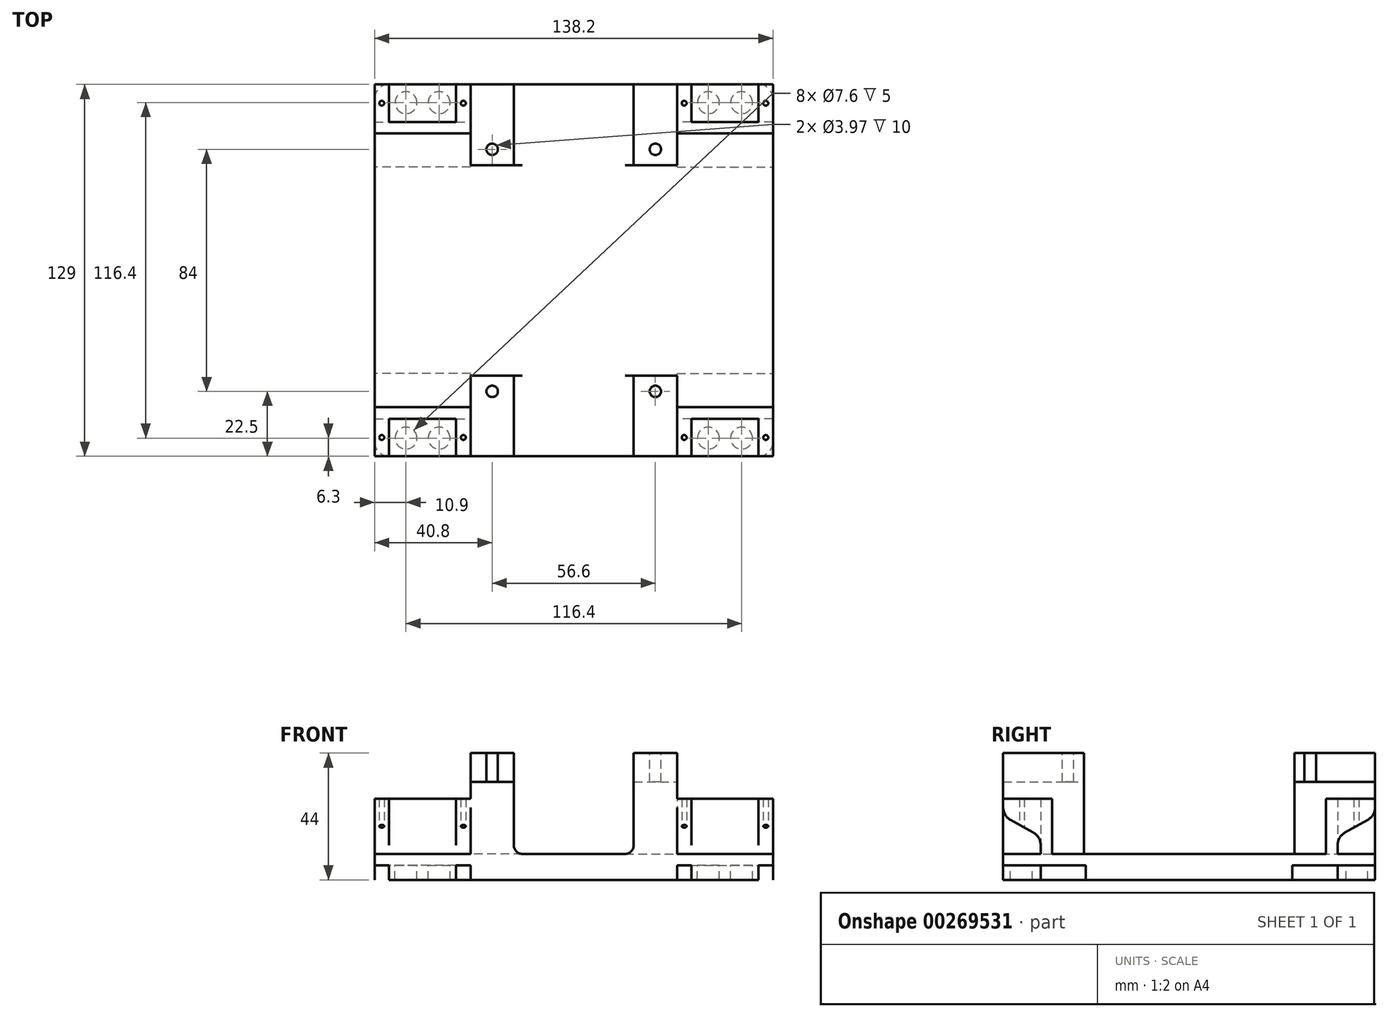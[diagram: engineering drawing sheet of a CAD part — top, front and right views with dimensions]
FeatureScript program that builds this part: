
annotation { "Feature Type Name" : "Feature", "Feature Type Description" : "" }
export const myFeature = defineFeature(function(context is Context, id is Id, definition is map)
    precondition{}
    {
        {
            var Q0;
            Q0=qCreatedBy(makeId("Top.planeOp"),FACE);
            var sketch = newSketch(context, id + "F0", { "sketchPlane" : qUnion([Q0])});
            skLineSegment(sketch, "E0.bottom", {"start": v(16.65, 8.5) * mm, "end": v(-16.65, 8.5) * mm});
            skLineSegment(sketch, "E0.top", {"start": v(16.65, -8.5) * mm, "end": v(-16.65, -8.5) * mm});
            skLineSegment(sketch, "E0.left", {"start": v(16.65, 8.5) * mm, "end": v(16.65, -8.5) * mm});
            skLineSegment(sketch, "E0.right", {"start": v(-16.65, 8.5) * mm, "end": v(-16.65, -8.5) * mm});
            skPoint(sketch, "E0.middle", {"position": v(0, 0) * mm});
            skLineSegment(sketch, "E1", {"start": v(11.65, -8.5) * mm, "end": v(11.65, 8.5) * mm});
            skLineSegment(sketch, "E2", {"start": v(-11.65, -8.5) * mm, "end": v(-11.65, 8.5) * mm});
            skLineSegment(sketch, "E3", {"start": v(-11.65, 4.5) * mm, "end": v(11.65, 4.5) * mm});
            skCircle(sketch, "E4", {"center": v(14.15, -2) * mm, "radius": 0.85 * mm});
            skCircle(sketch, "E5", {"center": v(-14.15, -2) * mm, "radius": 0.85 * mm});
            skCircle(sketch, "E6", {"center": v(-5.75, -2.2) * mm, "radius": 3.8 * mm});
            skCircle(sketch, "E7.MirrorC", {"center": v(5.75, -2.2) * mm, "radius": 3.8 * mm});
            skLineSegment(sketch, "E8.bottom", {"start": v(-16.65, 8.5) * mm, "end": v(-33.65, 8.5) * mm});
            skLineSegment(sketch, "E8.top", {"start": v(-16.65, -8.5) * mm, "end": v(-33.65, -8.5) * mm});
            skLineSegment(sketch, "E8.right", {"start": v(-33.65, 8.5) * mm, "end": v(-33.65, -8.5) * mm});
            skLineSegment(sketch, "E9.bottom", {"start": v(-16.65, 8.5) * mm, "end": v(16.65, 8.5) * mm});
            skLineSegment(sketch, "E9.top", {"start": v(-16.65, 25.5) * mm, "end": v(16.65, 25.5) * mm});
            skLineSegment(sketch, "E9.left", {"start": v(-16.65, 8.5) * mm, "end": v(-16.65, 25.5) * mm});
            skLineSegment(sketch, "E9.right", {"start": v(16.65, 8.5) * mm, "end": v(16.65, 25.5) * mm});
            skCircle(sketch, "E10", {"center": v(-25.15, 0) * mm, "radius": 3 * mm});
            skPoint(sketch, "E10.centerSnap0", {"position": v(-25.15, -8.5) * mm});
            skCircle(sketch, "E11", {"center": v(-8.33, 17) * mm, "radius": 3 * mm});
            skPoint(sketch, "E11.centerSnap0", {"position": v(-16.65, 17) * mm});
            skLineSegment(sketch, "E12", {"start": v(0, 25.5) * mm, "end": v(0, 8.5) * mm});
            skCircle(sketch, "E13.MirrorC", {"center": v(8.33, 17) * mm, "radius": 3 * mm});
            skSolve(sketch);
        }
        {
            var Q0;
            Q0=qCreatedBy(makeId("Front.planeOp"),FACE);
            var sketch = newSketch(context, id + "F1", { "sketchPlane" : qUnion([Q0])});
            skLineSegment(sketch, "E14.bottom", {"start": v(-16.65, 0) * mm, "end": v(16.65, 0) * mm});
            skLineSegment(sketch, "E14.top", {"start": v(-16.65, 23.2) * mm, "end": v(16.65, 23.2) * mm});
            skLineSegment(sketch, "E14.left", {"start": v(-16.65, 0) * mm, "end": v(-16.65, 23.2) * mm});
            skLineSegment(sketch, "E14.right", {"start": v(16.65, 0) * mm, "end": v(16.65, 23.2) * mm});
            skLineSegment(sketch, "E15", {"start": v(-16.65, 4) * mm, "end": v(16.65, 4) * mm});
            skLineSegment(sketch, "E16", {"start": v(11.65, 0) * mm, "end": v(11.65, 23.2) * mm});
            skLineSegment(sketch, "E17", {"start": v(-11.65, 0) * mm, "end": v(-11.65, 23.2) * mm});
            skLineSegment(sketch, "E18", {"start": v(16.65, 10) * mm, "end": v(11.65, 10) * mm});
            skLineSegment(sketch, "E19", {"start": v(-11.65, 10) * mm, "end": v(-16.65, 10) * mm});
            skLineSegment(sketch, "E20", {"start": v(11.65, 17.2) * mm, "end": v(16.65, 17.2) * mm});
            skLineSegment(sketch, "E21", {"start": v(-11.65, 17.2) * mm, "end": v(-16.65, 17.2) * mm});
            skSolve(sketch);
        }
        {
            var Q0;
            Q0=qCreatedBy(makeId("Right.planeOp"),FACE);
            var sketch = newSketch(context, id + "F2", { "sketchPlane" : qUnion([Q0])});
            skLineSegment(sketch, "E22.bottom", {"start": v(-8.5, 0) * mm, "end": v(8.5, 0) * mm});
            skLineSegment(sketch, "E22.top", {"start": v(-8.5, 23.2) * mm, "end": v(8.5, 23.2) * mm});
            skLineSegment(sketch, "E22.left", {"start": v(-8.5, 20.15) * mm, "end": v(-8.5, 23.2) * mm});
            skLineSegment(sketch, "E22.right", {"start": v(8.5, 0) * mm, "end": v(8.5, 23.2) * mm});
            skLineSegment(sketch, "E23", {"start": v(4.5, 7.05) * mm, "end": v(4.5, 0) * mm});
            skLineSegment(sketch, "E24", {"start": v(4.5, 17.2) * mm, "end": v(-8.5, 17.2) * mm});
            skLineSegment(sketch, "E25", {"start": v(4.5, 4) * mm, "end": v(-8.5, 4) * mm});
            skLineSegment(sketch, "E26", {"start": v(-8.5, 10) * mm, "end": v(4.5, 10) * mm});
            skLineSegment(sketch, "E27", {"start": v(-5.92, 15.77) * mm, "end": v(1.92, 11.43) * mm});
            skArc(sketch, "E28.filletArc", {"start": v(-8.5, 20.15) * mm, "mid": v(-7.8, 17.6) * mm, "end": v(-5.92, 15.77) * mm});
            skArc(sketch, "E29.filletArc", {"start": v(4.5, 7.05) * mm, "mid": v(3.8, 9.6) * mm, "end": v(1.92, 11.43) * mm});
            skLineSegment(sketch, "E30", {"start": v(-8.5, 20.15) * mm, "end": v(-8.5, 0) * mm});
            skSolve(sketch);
        }
        {
            var Q0;
            {var subQ0=sQuery(id+"F1.wireOp",EDGE,"E19");Q0=makeQuery(id+"F1.imprint","IMPRINT",FACE,{"disambiguationData":[TD([[makeQuery(id+"F1.imprint","IMPRINT",EDGE,{"derivedFrom":subQ0}),-1.0]])]});}
            var Q1;
            {var subQ5=sQuery(id+"F1.wireOp",EDGE,"E21");Q1=makeQuery(id+"F1.imprint","IMPRINT",FACE,{"disambiguationData":[TD([[makeQuery(id+"F1.imprint","IMPRINT",EDGE,{"derivedFrom":subQ5}),-1.0]])]});}
            var Q2;
            {var subQ3=sQuery(id+"F1.wireOp",EDGE,"E19");Q2=makeQuery(id+"F1.imprint","IMPRINT",FACE,{"disambiguationData":[TD([[makeQuery(id+"F1.imprint","IMPRINT",EDGE,{"derivedFrom":subQ3}),1.0]])]});}
            var Q3;
            {var subQ0=sQuery(id+"F1.wireOp",EDGE,"E14.left");var subQ1=sQuery(id+"F1.wireOp",EDGE,"E14.bottom");var subQ2=makeQuery(id+"F1.imprint","INTERSECT",VERTEX,{"derivedFrom":[subQ1,subQ0]});Q3=makeQuery(id+"F1.imprint","IMPRINT",FACE,{"disambiguationData":[TD([[makeQuery(id+"F1.imprint","IMPRINT",EDGE,{"disambiguationData":[TD([[subQ2,-1.0]])],"derivedFrom":subQ1}),1.0]])]});}
            var Q4;
            {var subQ0=sQuery(id+"F1.wireOp",EDGE,"E16");var subQ1=sQuery(id+"F1.wireOp",EDGE,"E14.bottom");var subQ2=makeQuery(id+"F1.imprint","INTERSECT",VERTEX,{"derivedFrom":[subQ1,subQ0]});Q4=makeQuery(id+"F1.imprint","IMPRINT",FACE,{"disambiguationData":[TD([[makeQuery(id+"F1.imprint","IMPRINT",EDGE,{"disambiguationData":[TD([[subQ2,1.0]])],"derivedFrom":subQ1}),1.0]])]});}
            var Q5;
            {var subQ0=sQuery(id+"F1.wireOp",EDGE,"E14.right");var subQ1=sQuery(id+"F1.wireOp",EDGE,"E14.bottom");var subQ2=makeQuery(id+"F1.imprint","INTERSECT",VERTEX,{"derivedFrom":[subQ1,subQ0]});Q5=makeQuery(id+"F1.imprint","IMPRINT",FACE,{"disambiguationData":[TD([[makeQuery(id+"F1.imprint","IMPRINT",EDGE,{"disambiguationData":[TD([[subQ2,1.0]])],"derivedFrom":subQ1}),1.0]])]});}
            var Q6;
            {var subQ3=sQuery(id+"F1.wireOp",EDGE,"E18");Q6=makeQuery(id+"F1.imprint","IMPRINT",FACE,{"disambiguationData":[TD([[makeQuery(id+"F1.imprint","IMPRINT",EDGE,{"derivedFrom":subQ3}),1.0]])]});}
            var Q7;
            {var subQ0=sQuery(id+"F1.wireOp",EDGE,"E18");Q7=makeQuery(id+"F1.imprint","IMPRINT",FACE,{"disambiguationData":[TD([[makeQuery(id+"F1.imprint","IMPRINT",EDGE,{"derivedFrom":subQ0}),-1.0]])]});}
            var Q8;
            {var subQ5=sQuery(id+"F1.wireOp",EDGE,"E20");Q8=makeQuery(id+"F1.imprint","IMPRINT",FACE,{"disambiguationData":[TD([[makeQuery(id+"F1.imprint","IMPRINT",EDGE,{"derivedFrom":subQ5}),1.0]])]});}
            extrude(context, id + "F3", {"entities" : qUnion([Q0, Q1, Q2, Q3, Q4, Q5, Q6, Q7, Q8]), "endBound" : BoundingType.SYMMETRIC, "depth" : 17 * mm});
        }
        {
            var Q0;
            {var subQ5=sQuery(id+"F0.wireOp",EDGE,"E3");Q0=makeQuery(id+"F0.imprint","IMPRINT",FACE,{"disambiguationData":[TD([[makeQuery(id+"F0.imprint","IMPRINT",EDGE,{"derivedFrom":subQ5}),1.0]])]});}
            extrude(context, id + "F4", {"entities" : qUnion([Q0]), "operationType" : NewBodyOperationType.ADD, "depth" : 23.2 * mm});
        }
        {
            var Q0;
            {var subQ0=sQuery(id+"F2.wireOp",EDGE,"E27");Q0=makeQuery(id+"F2.imprint","IMPRINT",FACE,{"disambiguationData":[TD([[makeQuery(id+"F2.imprint","IMPRINT",EDGE,{"derivedFrom":subQ0}),-1.0]])]});}
            var Q1;
            {var subQ0=sQuery(id+"F2.wireOp",EDGE,"E30");var subQ1=sQuery(id+"F2.wireOp",EDGE,"E24");var subQ2=makeQuery(id+"F2.imprint","INTERSECT",VERTEX,{"derivedFrom":[subQ1,subQ0]});Q1=makeQuery(id+"F2.imprint","IMPRINT",FACE,{"disambiguationData":[TD([[makeQuery(id+"F2.imprint","IMPRINT",EDGE,{"disambiguationData":[TD([[subQ2,1.0]])],"derivedFrom":subQ1}),-1.0]])]});}
            var Q2;
            {var subQ5=sQuery(id+"F2.wireOp",EDGE,"E25");Q2=makeQuery(id+"F2.imprint","IMPRINT",FACE,{"disambiguationData":[TD([[makeQuery(id+"F2.imprint","IMPRINT",EDGE,{"derivedFrom":subQ5}),-1.0]])]});}
            extrude(context, id + "F5", {"entities" : qUnion([Q0, Q1, Q2]), "operationType" : NewBodyOperationType.REMOVE, "endBound" : BoundingType.SYMMETRIC, "oppositeDirection" : true, "depth" : 36.2 * mm});
        }
        {
            var Q0;
            Q0=makeQuery(id+"F0.imprint","IMPRINT",FACE,{"disambiguationData":[TD([[makeQuery(id+"F0.imprint","IMPRINT",EDGE,{"derivedFrom":sQuery(id+"F0.wireOp",EDGE,"E4")}),1.0]])]});
            var Q1;
            Q1=makeQuery(id+"F0.imprint","IMPRINT",FACE,{"disambiguationData":[TD([[makeQuery(id+"F0.imprint","IMPRINT",EDGE,{"derivedFrom":sQuery(id+"F0.wireOp",EDGE,"E5")}),1.0]])]});
            extrude(context, id + "F6", {"entities" : qUnion([Q0, Q1]), "operationType" : NewBodyOperationType.REMOVE, "depth" : 25 * mm, "hasSecondDirection" : true, "secondDirectionOppositeDirection" : false, "secondDirectionDepth" : 4.3 * mm});
        }
        {
            var Q0;
            Q0=makeQuery(id+"F0.imprint","IMPRINT",FACE,{"disambiguationData":[TD([[makeQuery(id+"F0.imprint","IMPRINT",EDGE,{"derivedFrom":sQuery(id+"F0.wireOp",EDGE,"E7.MirrorC")}),-1.0]])]});
            extrude(context, id + "F7", {"entities" : qUnion([Q0]), "operationType" : NewBodyOperationType.ADD, "oppositeDirection" : true, "depth" : 5 * mm});
        }
        {
            var Q0;
            Q0=makeQuery(id+"F3.opExtrude","SWEPT_BODY",BODY,{"disambiguationData":[OSD([sQuery(id+"F1.wireOp",EDGE,"E14.bottom"),sQuery(id+"F1.wireOp",EDGE,"E14.top"),sQuery(id+"F1.wireOp",EDGE,"E14.left"),sQuery(id+"F1.wireOp",EDGE,"E14.right"),sQuery(id+"F1.wireOp",EDGE,"E15"),sQuery(id+"F1.wireOp",EDGE,"E16"),sQuery(id+"F1.wireOp",EDGE,"E17")])]});
            transform(context, id + "F8", {"entities" : qUnion([Q0]), "transformType" : TransformType.TRANSLATION_3D, "dx" : 52.45 * mm, "dy" : -56 * mm, "dz" : 0 * mm, "makeCopy" : false});
        }
        {
            var Q0;
            Q0=makeQuery(id+"F3.opExtrude","SWEPT_BODY",BODY,{"disambiguationData":[OSD([sQuery(id+"F1.wireOp",EDGE,"E14.bottom"),sQuery(id+"F1.wireOp",EDGE,"E14.top"),sQuery(id+"F1.wireOp",EDGE,"E14.left"),sQuery(id+"F1.wireOp",EDGE,"E14.right"),sQuery(id+"F1.wireOp",EDGE,"E15"),sQuery(id+"F1.wireOp",EDGE,"E16"),sQuery(id+"F1.wireOp",EDGE,"E17")])]});
            var Q1;
            Q1=qCreatedBy(makeId("Front.planeOp"),FACE);
            mirror(context, id + "F9", {"entities" : qUnion([Q0]), "mirrorPlane" : qUnion([Q1])});
        }
        {
            var Q0;
            Q0=makeQuery(id+"F9.opPattern","COPY",BODY,{"derivedFrom":makeQuery(id+"F3.opExtrude","SWEPT_BODY",BODY,{"disambiguationData":[OSD([sQuery(id+"F1.wireOp",EDGE,"E14.bottom"),sQuery(id+"F1.wireOp",EDGE,"E14.top"),sQuery(id+"F1.wireOp",EDGE,"E14.left"),sQuery(id+"F1.wireOp",EDGE,"E14.right"),sQuery(id+"F1.wireOp",EDGE,"E15"),sQuery(id+"F1.wireOp",EDGE,"E16"),sQuery(id+"F1.wireOp",EDGE,"E17")])]}),"instanceName":"1"});
            var Q1;
            Q1=makeQuery(id+"F3.opExtrude","SWEPT_BODY",BODY,{"disambiguationData":[OSD([sQuery(id+"F1.wireOp",EDGE,"E14.bottom"),sQuery(id+"F1.wireOp",EDGE,"E14.top"),sQuery(id+"F1.wireOp",EDGE,"E14.left"),sQuery(id+"F1.wireOp",EDGE,"E14.right"),sQuery(id+"F1.wireOp",EDGE,"E15"),sQuery(id+"F1.wireOp",EDGE,"E16"),sQuery(id+"F1.wireOp",EDGE,"E17")])]});
            var Q2;
            Q2=qCreatedBy(makeId("Right.planeOp"),FACE);
            mirror(context, id + "F10", {"entities" : qUnion([Q0, Q1]), "mirrorPlane" : qUnion([Q2])});
        }
        {
            var Q0;
            Q0=qCreatedBy(makeId("Top.planeOp"),FACE);
            var sketch = newSketch(context, id + "F11", { "sketchPlane" : qUnion([Q0])});
            skLineSegment(sketch, "E31.bottom", {"start": v(64.5, 64.5) * mm, "end": v(-64.5, 64.5) * mm});
            skLineSegment(sketch, "E31.top", {"start": v(64.5, -64.5) * mm, "end": v(-64.5, -64.5) * mm});
            skLineSegment(sketch, "E31.left", {"start": v(64.5, 64.5) * mm, "end": v(64.5, -64.5) * mm});
            skLineSegment(sketch, "E31.right", {"start": v(-64.5, 64.5) * mm, "end": v(-64.5, -64.5) * mm});
            skPoint(sketch, "E31.middle", {"position": v(0, 0) * mm});
            skLineSegment(sketch, "E32.bottom", {"start": v(-69.1, -64.5) * mm, "end": v(69.1, -64.5) * mm});
            skLineSegment(sketch, "E32.top", {"start": v(-69.1, 64.5) * mm, "end": v(69.1, 64.5) * mm});
            skLineSegment(sketch, "E32.left", {"start": v(-69.1, -64.5) * mm, "end": v(-69.1, 64.5) * mm});
            skLineSegment(sketch, "E32.right", {"start": v(69.1, -64.5) * mm, "end": v(69.1, 64.5) * mm});
            skLineSegment(sketch, "E33.bottom", {"start": v(-35.8, -47.5) * mm, "end": v(-69.1, -47.5) * mm});
            skLineSegment(sketch, "E33.top", {"start": v(-35.8, -64.5) * mm, "end": v(-69.1, -64.5) * mm});
            skLineSegment(sketch, "E33.left", {"start": v(-35.8, -47.5) * mm, "end": v(-35.8, -64.5) * mm});
            skLineSegment(sketch, "E33.right", {"start": v(-69.1, -47.5) * mm, "end": v(-69.1, -64.5) * mm});
            skLineSegment(sketch, "E34.bottom", {"start": v(69.1, -64.5) * mm, "end": v(35.8, -64.5) * mm});
            skLineSegment(sketch, "E34.top", {"start": v(69.1, -47.5) * mm, "end": v(35.8, -47.5) * mm});
            skLineSegment(sketch, "E34.left", {"start": v(69.1, -64.5) * mm, "end": v(69.1, -47.5) * mm});
            skLineSegment(sketch, "E34.right", {"start": v(35.8, -64.5) * mm, "end": v(35.8, -47.5) * mm});
            skLineSegment(sketch, "E35.bottom", {"start": v(69.1, 64.5) * mm, "end": v(35.8, 64.5) * mm});
            skLineSegment(sketch, "E35.top", {"start": v(69.1, 47.5) * mm, "end": v(35.8, 47.5) * mm});
            skLineSegment(sketch, "E35.left", {"start": v(69.1, 64.5) * mm, "end": v(69.1, 47.5) * mm});
            skLineSegment(sketch, "E35.right", {"start": v(35.8, 64.5) * mm, "end": v(35.8, 47.5) * mm});
            skLineSegment(sketch, "E36.bottom", {"start": v(-69.1, 64.5) * mm, "end": v(-35.8, 64.5) * mm});
            skLineSegment(sketch, "E36.top", {"start": v(-69.1, 47.5) * mm, "end": v(-35.8, 47.5) * mm});
            skLineSegment(sketch, "E36.left", {"start": v(-69.1, 64.5) * mm, "end": v(-69.1, 47.5) * mm});
            skLineSegment(sketch, "E36.right", {"start": v(-35.8, 64.5) * mm, "end": v(-35.8, 47.5) * mm});
            skLineSegment(sketch, "E37.bottom", {"start": v(-35.8, 47.5) * mm, "end": v(-20.8, 47.5) * mm});
            skLineSegment(sketch, "E37.top", {"start": v(-35.8, 36.5) * mm, "end": v(-20.8, 36.5) * mm});
            skLineSegment(sketch, "E37.left", {"start": v(-35.8, 47.5) * mm, "end": v(-35.8, 36.5) * mm});
            skLineSegment(sketch, "E37.right", {"start": v(-20.8, 47.5) * mm, "end": v(-20.8, 36.5) * mm});
            skLineSegment(sketch, "E38.MirrorCS", {"start": v(20.8, 47.5) * mm, "end": v(20.8, 36.5) * mm});
            skLineSegment(sketch, "E39.MirrorCS", {"start": v(35.8, 47.5) * mm, "end": v(20.8, 47.5) * mm});
            skLineSegment(sketch, "E40.MirrorCS", {"start": v(20.8, -47.5) * mm, "end": v(20.8, -36.5) * mm});
            skLineSegment(sketch, "E41.MirrorCS", {"start": v(35.8, -47.5) * mm, "end": v(20.8, -47.5) * mm});
            skLineSegment(sketch, "E42.MirrorCS", {"start": v(-20.8, -47.5) * mm, "end": v(-20.8, -36.5) * mm});
            skLineSegment(sketch, "E43.MirrorCS", {"start": v(-35.8, -47.5) * mm, "end": v(-20.8, -47.5) * mm});
            skLineSegment(sketch, "E44.MirrorCS", {"start": v(-35.8, -47.5) * mm, "end": v(-35.8, -36.5) * mm});
            skLineSegment(sketch, "E45.MirrorCS", {"start": v(-35.8, -36.5) * mm, "end": v(-20.8, -36.5) * mm});
            skLineSegment(sketch, "E46", {"start": v(-20.8, -47.5) * mm, "end": v(-20.8, -64.5) * mm});
            skLineSegment(sketch, "E47", {"start": v(20.8, -47.5) * mm, "end": v(20.8, -64.5) * mm});
            skLineSegment(sketch, "E48", {"start": v(20.8, 47.5) * mm, "end": v(20.8, 64.5) * mm});
            skLineSegment(sketch, "E49", {"start": v(-20.8, 47.5) * mm, "end": v(-20.8, 64.5) * mm});
            skLineSegment(sketch, "E50", {"start": v(-35.8, -36.5) * mm, "end": v(-35.8, 36.5) * mm});
            skLineSegment(sketch, "E51", {"start": v(20.8, -36.5) * mm, "end": v(20.8, 36.5) * mm});
            skLineSegment(sketch, "E52.top", {"start": v(35.8, -36.5) * mm, "end": v(20.8, -36.5) * mm});
            skLineSegment(sketch, "E52.left", {"start": v(35.8, -47.5) * mm, "end": v(35.8, -36.5) * mm});
            skLineSegment(sketch, "E53.top", {"start": v(35.8, 36.5) * mm, "end": v(20.8, 36.5) * mm});
            skLineSegment(sketch, "E53.left", {"start": v(35.8, 47.5) * mm, "end": v(35.8, 36.5) * mm});
            skLineSegment(sketch, "E54", {"start": v(35.8, -35.8) * mm, "end": v(64.5, -35.8) * mm});
            skLineSegment(sketch, "E55", {"start": v(35.8, -35.8) * mm, "end": v(35.8, -36.5) * mm});
            skLineSegment(sketch, "E56", {"start": v(64.5, -35.8) * mm, "end": v(69.1, -35.8) * mm});
            skLineSegment(sketch, "E57.MirrorCS", {"start": v(64.5, 35.8) * mm, "end": v(69.1, 35.8) * mm});
            skLineSegment(sketch, "E58.MirrorCS", {"start": v(35.8, 35.8) * mm, "end": v(35.8, 36.5) * mm});
            skLineSegment(sketch, "E59.MirrorCS", {"start": v(35.8, 35.8) * mm, "end": v(64.5, 35.8) * mm});
            skLineSegment(sketch, "E60.MirrorCS", {"start": v(-35.8, 35.8) * mm, "end": v(-64.5, 35.8) * mm});
            skLineSegment(sketch, "E61.MirrorCS", {"start": v(-64.5, 35.8) * mm, "end": v(-69.1, 35.8) * mm});
            skLineSegment(sketch, "E62.MirrorCS", {"start": v(-35.8, 35.8) * mm, "end": v(-35.8, 36.5) * mm});
            skLineSegment(sketch, "E63.MirrorCS", {"start": v(-35.8, -35.8) * mm, "end": v(-64.5, -35.8) * mm});
            skLineSegment(sketch, "E64.MirrorCS", {"start": v(-64.5, -35.8) * mm, "end": v(-69.1, -35.8) * mm});
            skLineSegment(sketch, "E65.MirrorCS", {"start": v(-35.8, -35.8) * mm, "end": v(-35.8, -36.5) * mm});
            skSolve(sketch);
        }
        {
            var Q0;
            Q0=makeQuery(id+"F11.imprint","IMPRINT",FACE,{"disambiguationData":[TD([[makeQuery(id+"F11.imprint","IMPRINT",EDGE,{"derivedFrom":sQuery(id+"F11.wireOp",EDGE,"E37.top")}),-1.0]])]});
            var Q1;
            Q1=makeQuery(id+"F11.imprint","IMPRINT",FACE,{"disambiguationData":[TD([[makeQuery(id+"F11.imprint","IMPRINT",EDGE,{"derivedFrom":sQuery(id+"F11.wireOp",EDGE,"E42.MirrorCS")}),1.0]])]});
            var Q2;
            {var subQ0=sQuery(id+"F11.wireOp",EDGE,"E33.left");Q2=makeQuery(id+"F11.imprint","IMPRINT",FACE,{"disambiguationData":[TD([[makeQuery(id+"F11.imprint","IMPRINT",EDGE,{"derivedFrom":subQ0}),1.0]])]});}
            var Q3;
            {var subQ1=sQuery(id+"F11.wireOp",EDGE,"E44.MirrorCS");Q3=makeQuery(id+"F11.imprint","IMPRINT",FACE,{"disambiguationData":[TD([[makeQuery(id+"F11.imprint","IMPRINT",EDGE,{"derivedFrom":subQ1}),1.0]])]});}
            var Q4;
            {var subQ0=sQuery(id+"F11.wireOp",EDGE,"E64.MirrorCS");Q4=makeQuery(id+"F11.imprint","IMPRINT",FACE,{"disambiguationData":[TD([[makeQuery(id+"F11.imprint","IMPRINT",EDGE,{"derivedFrom":subQ0}),1.0]])]});}
            var Q5;
            Q5=makeQuery(id+"F11.imprint","IMPRINT",FACE,{"disambiguationData":[TD([[makeQuery(id+"F11.imprint","IMPRINT",EDGE,{"derivedFrom":sQuery(id+"F11.wireOp",EDGE,"E50")}),1.0]])]});
            var Q6;
            {var subQ0=sQuery(id+"F11.wireOp",EDGE,"E61.MirrorCS");Q6=makeQuery(id+"F11.imprint","IMPRINT",FACE,{"disambiguationData":[TD([[makeQuery(id+"F11.imprint","IMPRINT",EDGE,{"derivedFrom":subQ0}),1.0]])]});}
            var Q7;
            {var subQ0=sQuery(id+"F11.wireOp",EDGE,"E34.right");Q7=makeQuery(id+"F11.imprint","IMPRINT",FACE,{"disambiguationData":[TD([[makeQuery(id+"F11.imprint","IMPRINT",EDGE,{"derivedFrom":subQ0}),1.0]])]});}
            var Q8;
            Q8=makeQuery(id+"F11.imprint","IMPRINT",FACE,{"disambiguationData":[TD([[makeQuery(id+"F11.imprint","IMPRINT",EDGE,{"derivedFrom":sQuery(id+"F11.wireOp",EDGE,"E41.MirrorCS")}),-1.0]])]});
            var Q9;
            {var subQ0=sQuery(id+"F11.wireOp",EDGE,"E52.left");Q9=makeQuery(id+"F11.imprint","IMPRINT",FACE,{"disambiguationData":[TD([[makeQuery(id+"F11.imprint","IMPRINT",EDGE,{"derivedFrom":subQ0}),-1.0]])]});}
            var Q10;
            Q10=makeQuery(id+"F11.imprint","IMPRINT",FACE,{"disambiguationData":[TD([[makeQuery(id+"F11.imprint","IMPRINT",EDGE,{"derivedFrom":sQuery(id+"F11.wireOp",EDGE,"E51")}),-1.0]])]});
            var Q11;
            {var subQ0=sQuery(id+"F11.wireOp",EDGE,"E56");Q11=makeQuery(id+"F11.imprint","IMPRINT",FACE,{"disambiguationData":[TD([[makeQuery(id+"F11.imprint","IMPRINT",EDGE,{"derivedFrom":subQ0}),1.0]])]});}
            var Q12;
            {var subQ0=sQuery(id+"F11.wireOp",EDGE,"E56");Q12=makeQuery(id+"F11.imprint","IMPRINT",FACE,{"disambiguationData":[TD([[makeQuery(id+"F11.imprint","IMPRINT",EDGE,{"derivedFrom":subQ0}),-1.0]])]});}
            var Q13;
            {var subQ0=sQuery(id+"F11.wireOp",EDGE,"E35.right");Q13=makeQuery(id+"F11.imprint","IMPRINT",FACE,{"disambiguationData":[TD([[makeQuery(id+"F11.imprint","IMPRINT",EDGE,{"derivedFrom":subQ0}),-1.0]])]});}
            var Q14;
            Q14=makeQuery(id+"F11.imprint","IMPRINT",FACE,{"disambiguationData":[TD([[makeQuery(id+"F11.imprint","IMPRINT",EDGE,{"derivedFrom":sQuery(id+"F11.wireOp",EDGE,"E39.MirrorCS")}),1.0]])]});
            var Q15;
            {var subQ0=sQuery(id+"F11.wireOp",EDGE,"E53.left");Q15=makeQuery(id+"F11.imprint","IMPRINT",FACE,{"disambiguationData":[TD([[makeQuery(id+"F11.imprint","IMPRINT",EDGE,{"derivedFrom":subQ0}),1.0]])]});}
            var Q16;
            {var subQ0=sQuery(id+"F11.wireOp",EDGE,"E57.MirrorCS");Q16=makeQuery(id+"F11.imprint","IMPRINT",FACE,{"disambiguationData":[TD([[makeQuery(id+"F11.imprint","IMPRINT",EDGE,{"derivedFrom":subQ0}),1.0]])]});}
            var Q17;
            {var subQ0=sQuery(id+"F11.wireOp",EDGE,"E36.right");Q17=makeQuery(id+"F11.imprint","IMPRINT",FACE,{"disambiguationData":[TD([[makeQuery(id+"F11.imprint","IMPRINT",EDGE,{"derivedFrom":subQ0}),1.0]])]});}
            var Q18;
            Q18=makeQuery(id+"F11.imprint","IMPRINT",FACE,{"disambiguationData":[TD([[makeQuery(id+"F11.imprint","IMPRINT",EDGE,{"derivedFrom":sQuery(id+"F11.wireOp",EDGE,"E37.bottom")}),-1.0]])]});
            var Q19;
            {var subQ1=sQuery(id+"F11.wireOp",EDGE,"E37.left");Q19=makeQuery(id+"F11.imprint","IMPRINT",FACE,{"disambiguationData":[TD([[makeQuery(id+"F11.imprint","IMPRINT",EDGE,{"derivedFrom":subQ1}),-1.0]])]});}
            var Q20;
            {var subQ0=sQuery(id+"F11.wireOp",EDGE,"E61.MirrorCS");Q20=makeQuery(id+"F11.imprint","IMPRINT",FACE,{"disambiguationData":[TD([[makeQuery(id+"F11.imprint","IMPRINT",EDGE,{"derivedFrom":subQ0}),-1.0]])]});}
            extrude(context, id + "F12", {"entities" : qUnion([Q0, Q1, Q2, Q3, Q4, Q5, Q6, Q7, Q8, Q9, Q10, Q11, Q12, Q13, Q14, Q15, Q16, Q17, Q18, Q19, Q20]), "operationType" : NewBodyOperationType.ADD, "depth" : 4 * mm, "offsetDistance" : 25 * mm});
        }
        {
            var Q0;
            Q0=makeQuery(id+"F11.imprint","IMPRINT",FACE,{"disambiguationData":[TD([[makeQuery(id+"F11.imprint","IMPRINT",EDGE,{"derivedFrom":sQuery(id+"F11.wireOp",EDGE,"E37.top")}),-1.0]])]});
            var Q1;
            Q1=makeQuery(id+"F11.imprint","IMPRINT",FACE,{"disambiguationData":[TD([[makeQuery(id+"F11.imprint","IMPRINT",EDGE,{"derivedFrom":sQuery(id+"F11.wireOp",EDGE,"E50")}),1.0]])]});
            var Q2;
            {var subQ0=sQuery(id+"F11.wireOp",EDGE,"E61.MirrorCS");Q2=makeQuery(id+"F11.imprint","IMPRINT",FACE,{"disambiguationData":[TD([[makeQuery(id+"F11.imprint","IMPRINT",EDGE,{"derivedFrom":subQ0}),1.0]])]});}
            var Q3;
            Q3=makeQuery(id+"F11.imprint","IMPRINT",FACE,{"disambiguationData":[TD([[makeQuery(id+"F11.imprint","IMPRINT",EDGE,{"derivedFrom":sQuery(id+"F11.wireOp",EDGE,"E42.MirrorCS")}),1.0]])]});
            var Q4;
            {var subQ0=sQuery(id+"F11.wireOp",EDGE,"E33.left");Q4=makeQuery(id+"F11.imprint","IMPRINT",FACE,{"disambiguationData":[TD([[makeQuery(id+"F11.imprint","IMPRINT",EDGE,{"derivedFrom":subQ0}),1.0]])]});}
            var Q5;
            {var subQ0=sQuery(id+"F11.wireOp",EDGE,"E34.right");Q5=makeQuery(id+"F11.imprint","IMPRINT",FACE,{"disambiguationData":[TD([[makeQuery(id+"F11.imprint","IMPRINT",EDGE,{"derivedFrom":subQ0}),1.0]])]});}
            var Q6;
            Q6=makeQuery(id+"F11.imprint","IMPRINT",FACE,{"disambiguationData":[TD([[makeQuery(id+"F11.imprint","IMPRINT",EDGE,{"derivedFrom":sQuery(id+"F11.wireOp",EDGE,"E41.MirrorCS")}),-1.0]])]});
            var Q7;
            Q7=makeQuery(id+"F11.imprint","IMPRINT",FACE,{"disambiguationData":[TD([[makeQuery(id+"F11.imprint","IMPRINT",EDGE,{"derivedFrom":sQuery(id+"F11.wireOp",EDGE,"E51")}),-1.0]])]});
            var Q8;
            {var subQ0=sQuery(id+"F11.wireOp",EDGE,"E56");Q8=makeQuery(id+"F11.imprint","IMPRINT",FACE,{"disambiguationData":[TD([[makeQuery(id+"F11.imprint","IMPRINT",EDGE,{"derivedFrom":subQ0}),1.0]])]});}
            var Q9;
            Q9=makeQuery(id+"F11.imprint","IMPRINT",FACE,{"disambiguationData":[TD([[makeQuery(id+"F11.imprint","IMPRINT",EDGE,{"derivedFrom":sQuery(id+"F11.wireOp",EDGE,"E39.MirrorCS")}),1.0]])]});
            var Q10;
            {var subQ0=sQuery(id+"F11.wireOp",EDGE,"E35.right");Q10=makeQuery(id+"F11.imprint","IMPRINT",FACE,{"disambiguationData":[TD([[makeQuery(id+"F11.imprint","IMPRINT",EDGE,{"derivedFrom":subQ0}),-1.0]])]});}
            var Q11;
            {var subQ0=sQuery(id+"F11.wireOp",EDGE,"E36.right");Q11=makeQuery(id+"F11.imprint","IMPRINT",FACE,{"disambiguationData":[TD([[makeQuery(id+"F11.imprint","IMPRINT",EDGE,{"derivedFrom":subQ0}),1.0]])]});}
            var Q12;
            Q12=makeQuery(id+"F11.imprint","IMPRINT",FACE,{"disambiguationData":[TD([[makeQuery(id+"F11.imprint","IMPRINT",EDGE,{"derivedFrom":sQuery(id+"F11.wireOp",EDGE,"E37.bottom")}),-1.0]])]});
            extrude(context, id + "F13", {"entities" : qUnion([Q0, Q1, Q2, Q3, Q4, Q5, Q6, Q7, Q8, Q9, Q10, Q11, Q12]), "operationType" : NewBodyOperationType.ADD, "oppositeDirection" : true, "depth" : 5 * mm, "offsetDistance" : 25 * mm});
        }
        {
            var Q0;
            {var subQ0=sQuery(id+"F11.wireOp",EDGE,"E33.left");Q0=makeQuery(id+"F11.imprint","IMPRINT",FACE,{"disambiguationData":[TD([[makeQuery(id+"F11.imprint","IMPRINT",EDGE,{"derivedFrom":subQ0}),1.0]])]});}
            var Q1;
            Q1=makeQuery(id+"F11.imprint","IMPRINT",FACE,{"disambiguationData":[TD([[makeQuery(id+"F11.imprint","IMPRINT",EDGE,{"derivedFrom":sQuery(id+"F11.wireOp",EDGE,"E42.MirrorCS")}),1.0]])]});
            var Q2;
            Q2=makeQuery(id+"F11.imprint","IMPRINT",FACE,{"disambiguationData":[TD([[makeQuery(id+"F11.imprint","IMPRINT",EDGE,{"derivedFrom":sQuery(id+"F11.wireOp",EDGE,"E41.MirrorCS")}),-1.0]])]});
            var Q3;
            {var subQ0=sQuery(id+"F11.wireOp",EDGE,"E34.right");Q3=makeQuery(id+"F11.imprint","IMPRINT",FACE,{"disambiguationData":[TD([[makeQuery(id+"F11.imprint","IMPRINT",EDGE,{"derivedFrom":subQ0}),1.0]])]});}
            var Q4;
            Q4=makeQuery(id+"F11.imprint","IMPRINT",FACE,{"disambiguationData":[TD([[makeQuery(id+"F11.imprint","IMPRINT",EDGE,{"derivedFrom":sQuery(id+"F11.wireOp",EDGE,"E39.MirrorCS")}),1.0]])]});
            var Q5;
            {var subQ0=sQuery(id+"F11.wireOp",EDGE,"E35.right");Q5=makeQuery(id+"F11.imprint","IMPRINT",FACE,{"disambiguationData":[TD([[makeQuery(id+"F11.imprint","IMPRINT",EDGE,{"derivedFrom":subQ0}),-1.0]])]});}
            var Q6;
            Q6=makeQuery(id+"F11.imprint","IMPRINT",FACE,{"disambiguationData":[TD([[makeQuery(id+"F11.imprint","IMPRINT",EDGE,{"derivedFrom":sQuery(id+"F11.wireOp",EDGE,"E37.bottom")}),-1.0]])]});
            var Q7;
            {var subQ0=sQuery(id+"F11.wireOp",EDGE,"E36.right");Q7=makeQuery(id+"F11.imprint","IMPRINT",FACE,{"disambiguationData":[TD([[makeQuery(id+"F11.imprint","IMPRINT",EDGE,{"derivedFrom":subQ0}),1.0]])]});}
            extrude(context, id + "F14", {"entities" : qUnion([Q0, Q1, Q2, Q3, Q4, Q5, Q6, Q7]), "operationType" : NewBodyOperationType.ADD, "depth" : 39 * mm, "offsetDistance" : 25 * mm});
        }
        {
            var Q0;
            Q0=makeQuery(id+"F14.opExtrude","CAP_FACE",FACE,{"disambiguationData":[OSD([sQuery(id+"F11.wireOp",EDGE,"E32.top"),sQuery(id+"F11.wireOp",EDGE,"E36.right"),sQuery(id+"F11.wireOp",EDGE,"E37.top"),sQuery(id+"F11.wireOp",EDGE,"E37.left"),sQuery(id+"F11.wireOp",EDGE,"E37.right"),sQuery(id+"F11.wireOp",EDGE,"E49")])],"isStart":false});
            var sketch = newSketch(context, id + "F15", { "sketchPlane" : qUnion([Q0])});
            skLineSegment(sketch, "E66.bottom", {"start": v(-20.8, 64.5) * mm, "end": v(-35.8, 64.5) * mm});
            skLineSegment(sketch, "E66.top", {"start": v(-20.8, 36.5) * mm, "end": v(-35.8, 36.5) * mm});
            skLineSegment(sketch, "E66.left", {"start": v(-20.8, 64.5) * mm, "end": v(-20.8, 36.5) * mm});
            skLineSegment(sketch, "E66.right", {"start": v(-35.8, 64.5) * mm, "end": v(-35.8, 36.5) * mm});
            skLineSegment(sketch, "E67.MirrorCS", {"start": v(20.8, 64.5) * mm, "end": v(20.8, 36.5) * mm});
            skLineSegment(sketch, "E68.MirrorCS", {"start": v(20.8, 36.5) * mm, "end": v(35.8, 36.5) * mm});
            skLineSegment(sketch, "E69.MirrorCS", {"start": v(35.8, 64.5) * mm, "end": v(35.8, 36.5) * mm});
            skLineSegment(sketch, "E70.MirrorCS", {"start": v(20.8, 64.5) * mm, "end": v(35.8, 64.5) * mm});
            skLineSegment(sketch, "E71.MirrorCS", {"start": v(20.8, -36.5) * mm, "end": v(35.8, -36.5) * mm});
            skLineSegment(sketch, "E72.MirrorCS", {"start": v(35.8, -64.5) * mm, "end": v(35.8, -36.5) * mm});
            skLineSegment(sketch, "E73.MirrorCS", {"start": v(20.8, -64.5) * mm, "end": v(35.8, -64.5) * mm});
            skLineSegment(sketch, "E74.MirrorCS", {"start": v(20.8, -64.5) * mm, "end": v(20.8, -36.5) * mm});
            skLineSegment(sketch, "E75.MirrorCS", {"start": v(-20.8, -64.5) * mm, "end": v(-20.8, -36.5) * mm});
            skLineSegment(sketch, "E76.MirrorCS", {"start": v(-20.8, -36.5) * mm, "end": v(-35.8, -36.5) * mm});
            skLineSegment(sketch, "E77.MirrorCS", {"start": v(-35.8, -64.5) * mm, "end": v(-35.8, -36.5) * mm});
            skLineSegment(sketch, "E78.MirrorCS", {"start": v(-20.8, -64.5) * mm, "end": v(-35.8, -64.5) * mm});
            skCircle(sketch, "E79", {"center": v(-28.3, 42) * mm, "radius": 1.99 * mm});
            skCircle(sketch, "E80.MirrorC", {"center": v(28.3, 42) * mm, "radius": 1.99 * mm});
            skCircle(sketch, "E81.MirrorC", {"center": v(-28.3, -42) * mm, "radius": 1.99 * mm});
            skCircle(sketch, "E82.MirrorC", {"center": v(28.3, -42) * mm, "radius": 1.99 * mm});
            skSolve(sketch);
        }
        {
            var Q0;
            {var subQ0=makeQuery(id+"F5.boolean.opBoolean","MERGE",FACE,{"derivedFrom":[makeQuery(id+"F3.opExtrude","SWEPT_FACE",FACE,{"disambiguationData":[OSD([sQuery(id+"F1.wireOp",EDGE,"E15")])]}),makeQuery(id+"F5.opExtrude","SWEPT_FACE",FACE,{"disambiguationData":[OSD([sQuery(id+"F2.wireOp",EDGE,"E25")])]})]});var subQ1=makeQuery(id+"F9.opPattern","COPY",FACE,{"derivedFrom":subQ0,"instanceName":"1"});Q0=makeQuery(id+"F14.boolean.opBoolean","INTERSECT",EDGE,{"derivedFrom":[makeQuery(id+"F12.boolean.opBoolean","MERGE",FACE,{"derivedFrom":[subQ0,subQ1,makeQuery(id+"F10.opPattern","COPY",FACE,{"derivedFrom":subQ0,"instanceName":"1"}),makeQuery(id+"F10.opPattern","COPY",FACE,{"derivedFrom":subQ1,"instanceName":"1"}),makeQuery(id+"F12.opExtrude","CAP_FACE",FACE,{"disambiguationData":[OSD([sQuery(id+"F11.wireOp",EDGE,"E32.bottom"),sQuery(id+"F11.wireOp",EDGE,"E32.top"),sQuery(id+"F11.wireOp",EDGE,"E32.left"),sQuery(id+"F11.wireOp",EDGE,"E32.right"),sQuery(id+"F11.wireOp",EDGE,"E33.bottom"),sQuery(id+"F11.wireOp",EDGE,"E33.left"),sQuery(id+"F11.wireOp",EDGE,"E34.top"),sQuery(id+"F11.wireOp",EDGE,"E34.right"),sQuery(id+"F11.wireOp",EDGE,"E35.top"),sQuery(id+"F11.wireOp",EDGE,"E35.right"),sQuery(id+"F11.wireOp",EDGE,"E36.top"),sQuery(id+"F11.wireOp",EDGE,"E36.right")])],"isStart":false})]}),makeQuery(id+"F14.opExtrude","SWEPT_FACE",FACE,{"disambiguationData":[OSD([sQuery(id+"F11.wireOp",EDGE,"E47"),sQuery(id+"F11.wireOp",EDGE,"E40.MirrorCS")])]})]});}
            var Q1;
            {var subQ0=makeQuery(id+"F5.boolean.opBoolean","MERGE",FACE,{"derivedFrom":[makeQuery(id+"F3.opExtrude","SWEPT_FACE",FACE,{"disambiguationData":[OSD([sQuery(id+"F1.wireOp",EDGE,"E15")])]}),makeQuery(id+"F5.opExtrude","SWEPT_FACE",FACE,{"disambiguationData":[OSD([sQuery(id+"F2.wireOp",EDGE,"E25")])]})]});var subQ1=makeQuery(id+"F9.opPattern","COPY",FACE,{"derivedFrom":subQ0,"instanceName":"1"});Q1=makeQuery(id+"F14.boolean.opBoolean","INTERSECT",EDGE,{"derivedFrom":[makeQuery(id+"F12.boolean.opBoolean","MERGE",FACE,{"derivedFrom":[subQ0,subQ1,makeQuery(id+"F10.opPattern","COPY",FACE,{"derivedFrom":subQ0,"instanceName":"1"}),makeQuery(id+"F10.opPattern","COPY",FACE,{"derivedFrom":subQ1,"instanceName":"1"}),makeQuery(id+"F12.opExtrude","CAP_FACE",FACE,{"disambiguationData":[OSD([sQuery(id+"F11.wireOp",EDGE,"E32.bottom"),sQuery(id+"F11.wireOp",EDGE,"E32.top"),sQuery(id+"F11.wireOp",EDGE,"E32.left"),sQuery(id+"F11.wireOp",EDGE,"E32.right"),sQuery(id+"F11.wireOp",EDGE,"E33.bottom"),sQuery(id+"F11.wireOp",EDGE,"E33.left"),sQuery(id+"F11.wireOp",EDGE,"E34.top"),sQuery(id+"F11.wireOp",EDGE,"E34.right"),sQuery(id+"F11.wireOp",EDGE,"E35.top"),sQuery(id+"F11.wireOp",EDGE,"E35.right"),sQuery(id+"F11.wireOp",EDGE,"E36.top"),sQuery(id+"F11.wireOp",EDGE,"E36.right")])],"isStart":false})]}),makeQuery(id+"F14.opExtrude","SWEPT_FACE",FACE,{"disambiguationData":[OSD([sQuery(id+"F11.wireOp",EDGE,"E48"),sQuery(id+"F11.wireOp",EDGE,"E38.MirrorCS")])]})]});}
            var Q2;
            {var subQ0=makeQuery(id+"F5.boolean.opBoolean","MERGE",FACE,{"derivedFrom":[makeQuery(id+"F3.opExtrude","SWEPT_FACE",FACE,{"disambiguationData":[OSD([sQuery(id+"F1.wireOp",EDGE,"E15")])]}),makeQuery(id+"F5.opExtrude","SWEPT_FACE",FACE,{"disambiguationData":[OSD([sQuery(id+"F2.wireOp",EDGE,"E25")])]})]});var subQ1=makeQuery(id+"F9.opPattern","COPY",FACE,{"derivedFrom":subQ0,"instanceName":"1"});Q2=makeQuery(id+"F14.boolean.opBoolean","INTERSECT",EDGE,{"derivedFrom":[makeQuery(id+"F12.boolean.opBoolean","MERGE",FACE,{"derivedFrom":[subQ0,subQ1,makeQuery(id+"F10.opPattern","COPY",FACE,{"derivedFrom":subQ0,"instanceName":"1"}),makeQuery(id+"F10.opPattern","COPY",FACE,{"derivedFrom":subQ1,"instanceName":"1"}),makeQuery(id+"F12.opExtrude","CAP_FACE",FACE,{"disambiguationData":[OSD([sQuery(id+"F11.wireOp",EDGE,"E32.bottom"),sQuery(id+"F11.wireOp",EDGE,"E32.top"),sQuery(id+"F11.wireOp",EDGE,"E32.left"),sQuery(id+"F11.wireOp",EDGE,"E32.right"),sQuery(id+"F11.wireOp",EDGE,"E33.bottom"),sQuery(id+"F11.wireOp",EDGE,"E33.left"),sQuery(id+"F11.wireOp",EDGE,"E34.top"),sQuery(id+"F11.wireOp",EDGE,"E34.right"),sQuery(id+"F11.wireOp",EDGE,"E35.top"),sQuery(id+"F11.wireOp",EDGE,"E35.right"),sQuery(id+"F11.wireOp",EDGE,"E36.top"),sQuery(id+"F11.wireOp",EDGE,"E36.right")])],"isStart":false})]}),makeQuery(id+"F14.opExtrude","SWEPT_FACE",FACE,{"disambiguationData":[OSD([sQuery(id+"F11.wireOp",EDGE,"E37.right"),sQuery(id+"F11.wireOp",EDGE,"E49")])]})]});}
            var Q3;
            {var subQ0=makeQuery(id+"F5.boolean.opBoolean","MERGE",FACE,{"derivedFrom":[makeQuery(id+"F3.opExtrude","SWEPT_FACE",FACE,{"disambiguationData":[OSD([sQuery(id+"F1.wireOp",EDGE,"E15")])]}),makeQuery(id+"F5.opExtrude","SWEPT_FACE",FACE,{"disambiguationData":[OSD([sQuery(id+"F2.wireOp",EDGE,"E25")])]})]});var subQ1=makeQuery(id+"F9.opPattern","COPY",FACE,{"derivedFrom":subQ0,"instanceName":"1"});Q3=makeQuery(id+"F14.boolean.opBoolean","INTERSECT",EDGE,{"derivedFrom":[makeQuery(id+"F12.boolean.opBoolean","MERGE",FACE,{"derivedFrom":[subQ0,subQ1,makeQuery(id+"F10.opPattern","COPY",FACE,{"derivedFrom":subQ0,"instanceName":"1"}),makeQuery(id+"F10.opPattern","COPY",FACE,{"derivedFrom":subQ1,"instanceName":"1"}),makeQuery(id+"F12.opExtrude","CAP_FACE",FACE,{"disambiguationData":[OSD([sQuery(id+"F11.wireOp",EDGE,"E32.bottom"),sQuery(id+"F11.wireOp",EDGE,"E32.top"),sQuery(id+"F11.wireOp",EDGE,"E32.left"),sQuery(id+"F11.wireOp",EDGE,"E32.right"),sQuery(id+"F11.wireOp",EDGE,"E33.bottom"),sQuery(id+"F11.wireOp",EDGE,"E33.left"),sQuery(id+"F11.wireOp",EDGE,"E34.top"),sQuery(id+"F11.wireOp",EDGE,"E34.right"),sQuery(id+"F11.wireOp",EDGE,"E35.top"),sQuery(id+"F11.wireOp",EDGE,"E35.right"),sQuery(id+"F11.wireOp",EDGE,"E36.top"),sQuery(id+"F11.wireOp",EDGE,"E36.right")])],"isStart":false})]}),makeQuery(id+"F14.opExtrude","SWEPT_FACE",FACE,{"disambiguationData":[OSD([sQuery(id+"F11.wireOp",EDGE,"E42.MirrorCS"),sQuery(id+"F11.wireOp",EDGE,"E46")])]})]});}
            fillet(context, id + "F16", {"entities" : qUnion([Q0, Q1, Q2, Q3]), "radius" : 3 * mm, "tangentPropagation" : true, "allowEdgeOverflow" : false});
        }
        {
            var Q0;
            {var subQ0=sQuery(id+"F1.wireOp",EDGE,"E14.right");var subQ2=sQuery(id+"F1.wireOp",EDGE,"E14.bottom");Q0=makeQuery(id+"F5.boolean.opBoolean","SPLIT",EDGE,{"disambiguationData":[TD([makeQuery(id+"F3.opExtrude","SWEPT_FACE",FACE,{"disambiguationData":[OSD([subQ2])]})])],"derivedFrom":makeQuery(id+"F3.opExtrude","CAP_EDGE",EDGE,{"disambiguationData":[OSD([subQ0])],"isStart":false})});}
            var Q1;
            {var subQ0=sQuery(id+"F1.wireOp",EDGE,"E14.right");var subQ2=sQuery(id+"F1.wireOp",EDGE,"E14.bottom");Q1=makeQuery(id+"F9.opPattern","COPY",EDGE,{"derivedFrom":makeQuery(id+"F5.boolean.opBoolean","SPLIT",EDGE,{"disambiguationData":[TD([makeQuery(id+"F3.opExtrude","SWEPT_FACE",FACE,{"disambiguationData":[OSD([subQ2])]})])],"derivedFrom":makeQuery(id+"F3.opExtrude","CAP_EDGE",EDGE,{"disambiguationData":[OSD([subQ0])],"isStart":false})}),"instanceName":"1"});}
            var Q2;
            {var subQ0=sQuery(id+"F1.wireOp",EDGE,"E14.right");var subQ2=sQuery(id+"F1.wireOp",EDGE,"E14.bottom");Q2=makeQuery(id+"F10.opPattern","COPY",EDGE,{"derivedFrom":makeQuery(id+"F9.opPattern","COPY",EDGE,{"derivedFrom":makeQuery(id+"F5.boolean.opBoolean","SPLIT",EDGE,{"disambiguationData":[TD([makeQuery(id+"F3.opExtrude","SWEPT_FACE",FACE,{"disambiguationData":[OSD([subQ2])]})])],"derivedFrom":makeQuery(id+"F3.opExtrude","CAP_EDGE",EDGE,{"disambiguationData":[OSD([subQ0])],"isStart":false})}),"instanceName":"1"}),"instanceName":"1"});}
            var Q3;
            {var subQ0=sQuery(id+"F1.wireOp",EDGE,"E14.right");var subQ2=sQuery(id+"F1.wireOp",EDGE,"E14.bottom");Q3=makeQuery(id+"F10.opPattern","COPY",EDGE,{"derivedFrom":makeQuery(id+"F5.boolean.opBoolean","SPLIT",EDGE,{"disambiguationData":[TD([makeQuery(id+"F3.opExtrude","SWEPT_FACE",FACE,{"disambiguationData":[OSD([subQ2])]})])],"derivedFrom":makeQuery(id+"F3.opExtrude","CAP_EDGE",EDGE,{"disambiguationData":[OSD([subQ0])],"isStart":false})}),"instanceName":"1"});}
            fillet(context, id + "F17", {"entities" : qUnion([Q0, Q1, Q2, Q3]), "radius" : 5 * mm, "tangentPropagation" : true, "allowEdgeOverflow" : false});
        }
        {
            var Q0;
            Q0=makeQuery(id+"F15.imprint","IMPRINT",FACE,{"disambiguationData":[TD([[makeQuery(id+"F15.imprint","IMPRINT",EDGE,{"derivedFrom":sQuery(id+"F15.wireOp",EDGE,"E81.MirrorC")}),-1.0]])]});
            var Q1;
            Q1=makeQuery(id+"F15.imprint","IMPRINT",FACE,{"disambiguationData":[TD([[makeQuery(id+"F15.imprint","IMPRINT",EDGE,{"derivedFrom":sQuery(id+"F15.wireOp",EDGE,"E82.MirrorC")}),1.0]])]});
            var Q2;
            Q2=makeQuery(id+"F15.imprint","IMPRINT",FACE,{"disambiguationData":[TD([[makeQuery(id+"F15.imprint","IMPRINT",EDGE,{"derivedFrom":sQuery(id+"F15.wireOp",EDGE,"E80.MirrorC")}),-1.0]])]});
            var Q3;
            Q3=makeQuery(id+"F15.imprint","IMPRINT",FACE,{"disambiguationData":[TD([[makeQuery(id+"F15.imprint","IMPRINT",EDGE,{"derivedFrom":sQuery(id+"F15.wireOp",EDGE,"E79")}),1.0]])]});
            extrude(context, id + "F18", {"entities" : qUnion([Q0, Q1, Q2, Q3]), "operationType" : NewBodyOperationType.REMOVE, "oppositeDirection" : true, "depth" : 10 * mm, "offsetDistance" : 25 * mm});
        }
    });
